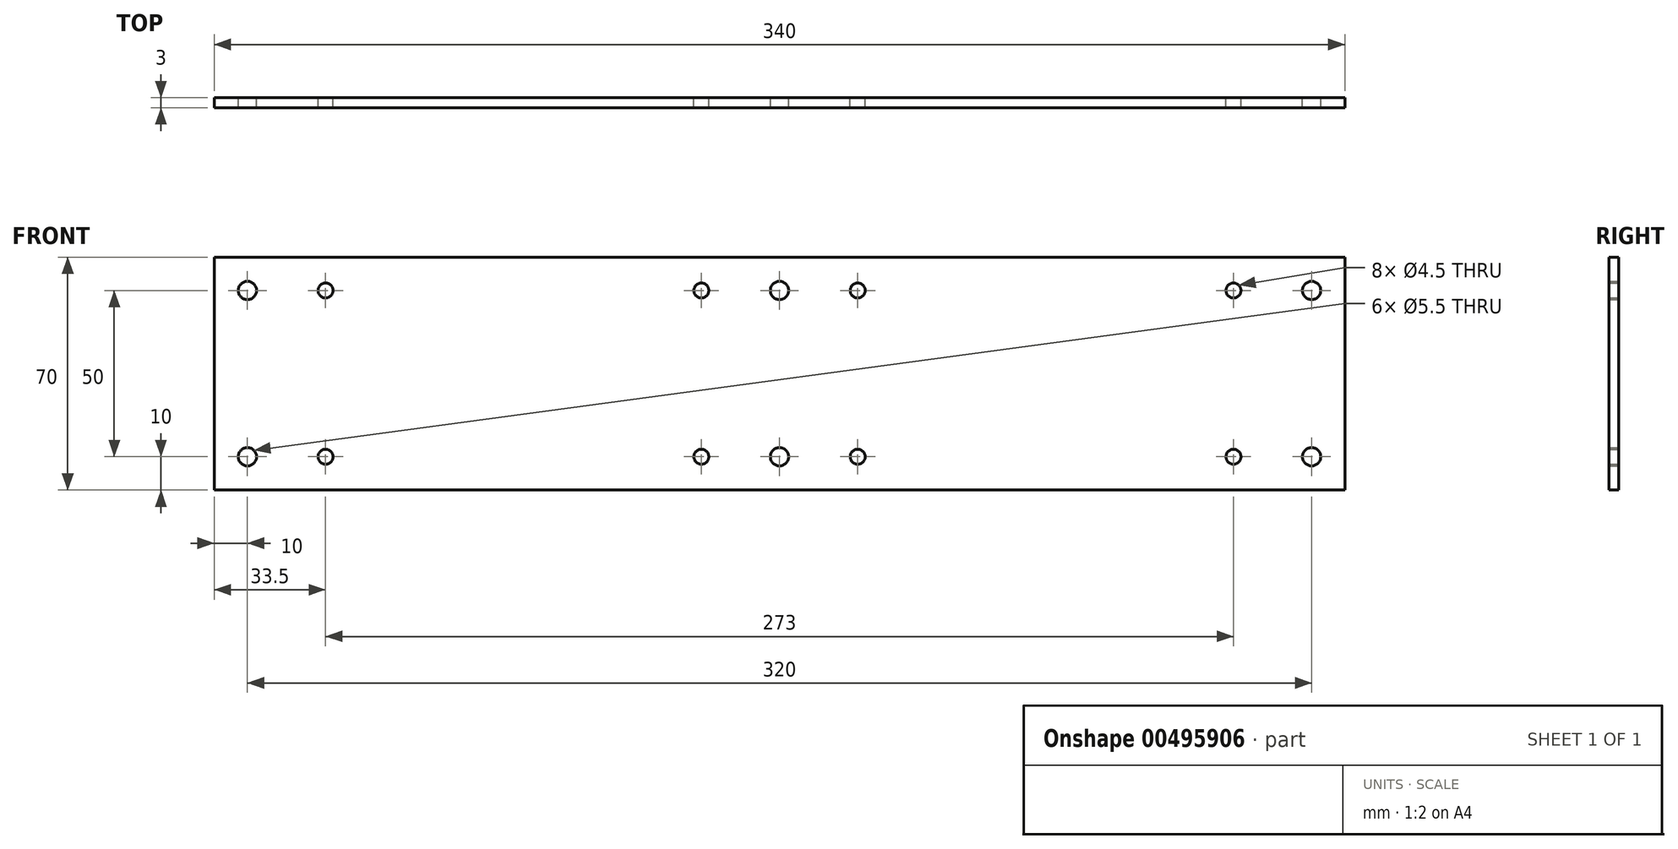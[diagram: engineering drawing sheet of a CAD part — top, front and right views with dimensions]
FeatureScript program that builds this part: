
annotation { "Feature Type Name" : "Feature", "Feature Type Description" : "" }
export const myFeature = defineFeature(function(context is Context, id is Id, definition is map)
    precondition{}
    {
        {
            var Q0;
            Q0=qCreatedBy(makeId("Front.planeOp"),FACE);
            var sketch = newSketch(context, id + "F0", { "sketchPlane" : qUnion([Q0])});
            skLineSegment(sketch, "E0.bottom", {"start": v(170, 35) * mm, "end": v(-170, 35) * mm});
            skLineSegment(sketch, "E0.top", {"start": v(170, -35) * mm, "end": v(-170, -35) * mm});
            skLineSegment(sketch, "E0.left", {"start": v(170, 35) * mm, "end": v(170, -35) * mm});
            skLineSegment(sketch, "E0.right", {"start": v(-170, 35) * mm, "end": v(-170, -35) * mm});
            skPoint(sketch, "E0.middle", {"position": v(0, 0) * mm});
            skLineSegment(sketch, "E1.0", {"start": v(160, 25) * mm, "end": v(-160, 25) * mm, "construction": true});
            skLineSegment(sketch, "E1.1", {"start": v(160, 25) * mm, "end": v(160, -25) * mm, "construction": true});
            skLineSegment(sketch, "E1.2", {"start": v(160, -25) * mm, "end": v(-160, -25) * mm, "construction": true});
            skLineSegment(sketch, "E1.3", {"start": v(-160, 25) * mm, "end": v(-160, -25) * mm, "construction": true});
            skCircle(sketch, "E2", {"center": v(-160, 25) * mm, "radius": 2.25 * mm});
            skCircle(sketch, "E3", {"center": v(-160, -25) * mm, "radius": 2.25 * mm});
            skCircle(sketch, "E4", {"center": v(0, 25) * mm, "radius": 2.25 * mm});
            skCircle(sketch, "E5", {"center": v(0, -25) * mm, "radius": 2.25 * mm});
            skCircle(sketch, "E6", {"center": v(160, -25) * mm, "radius": 2.25 * mm});
            skCircle(sketch, "E7", {"center": v(160, 25) * mm, "radius": 2.25 * mm});
            skCircle(sketch, "E8", {"center": v(-136.5, -25) * mm, "radius": 2.25 * mm});
            skCircle(sketch, "E9", {"center": v(-136.5, 25) * mm, "radius": 2.25 * mm});
            skCircle(sketch, "E10", {"center": v(23.5, 25) * mm, "radius": 2.25 * mm});
            skCircle(sketch, "E11", {"center": v(-23.5, 25) * mm, "radius": 2.25 * mm});
            skCircle(sketch, "E12", {"center": v(-23.5, -25) * mm, "radius": 2.25 * mm});
            skCircle(sketch, "E13", {"center": v(23.5, -25) * mm, "radius": 2.25 * mm});
            skCircle(sketch, "E14", {"center": v(136.5, -25) * mm, "radius": 2.25 * mm});
            skCircle(sketch, "E15", {"center": v(136.5, 25) * mm, "radius": 2.25 * mm});
            skSolve(sketch);
        }
        {
            var Q0;
            Q0=makeQuery(id+"F0.imprint","IMPRINT",FACE,{"disambiguationData":[TD([[makeQuery(id+"F0.imprint","IMPRINT",EDGE,{"derivedFrom":sQuery(id+"F0.wireOp",EDGE,"E0.bottom")}),1.0]])]});
            extrude(context, id + "F1", {"entities" : qUnion([Q0]), "depth" : 3 * mm});
        }
        {
            var Q0;
            Q0=sQuery(id+"F0.wireOp",VERTEX,"E1.0.end");
            var Q1;
            Q1=sQuery(id+"F0.wireOp",VERTEX,"E3.center");
            var Q2;
            Q2=sQuery(id+"F0.wireOp",VERTEX,"E4.center");
            var Q3;
            Q3=sQuery(id+"F0.wireOp",VERTEX,"E5.center");
            var Q4;
            Q4=sQuery(id+"F0.wireOp",VERTEX,"E1.1.start");
            var Q5;
            Q5=sQuery(id+"F0.wireOp",VERTEX,"E1.2.start");
            var Q6;
            Q6=makeQuery(id+"F1.opExtrude","SWEPT_BODY",BODY,{"disambiguationData":[OSD([sQuery(id+"F0.wireOp",EDGE,"E0.bottom"),sQuery(id+"F0.wireOp",EDGE,"E0.top"),sQuery(id+"F0.wireOp",EDGE,"E0.left"),sQuery(id+"F0.wireOp",EDGE,"E0.right"),sQuery(id+"F0.wireOp",EDGE,"E2"),sQuery(id+"F0.wireOp",EDGE,"E3"),sQuery(id+"F0.wireOp",EDGE,"E4"),sQuery(id+"F0.wireOp",EDGE,"E5"),sQuery(id+"F0.wireOp",EDGE,"E6"),sQuery(id+"F0.wireOp",EDGE,"E7"),sQuery(id+"F0.wireOp",EDGE,"E8"),sQuery(id+"F0.wireOp",EDGE,"E9"),sQuery(id+"F0.wireOp",EDGE,"E10"),sQuery(id+"F0.wireOp",EDGE,"E11"),sQuery(id+"F0.wireOp",EDGE,"E12"),sQuery(id+"F0.wireOp",EDGE,"E13"),sQuery(id+"F0.wireOp",EDGE,"E14"),sQuery(id+"F0.wireOp",EDGE,"E15")])]});
            hole(context, id + "F2", {"style" : HoleStyle.SIMPLE, "endStyle" : HoleEndStyle.THROUGH, "oppositeDirection" : true, "standardTappedOrClearance" : lookupTablePath({ "standard" : "ISO", "fit" : "Normal", "size" : "M5", "type" : "Clearance" }), "standardBlindInLast" : lookupTablePath({ "fit" : "Standard", "standard" : "ISO", "size" : "M5", "type" : "Clearance" }), "holeDiameter" : 5.5 * mm, "tappedDepth" : 12 * mm, "tapClearance" : 3, "locations" : qUnion([Q0, Q1, Q2, Q3, Q4, Q5]), "scope" : qUnion([Q6])});
        }
    });
